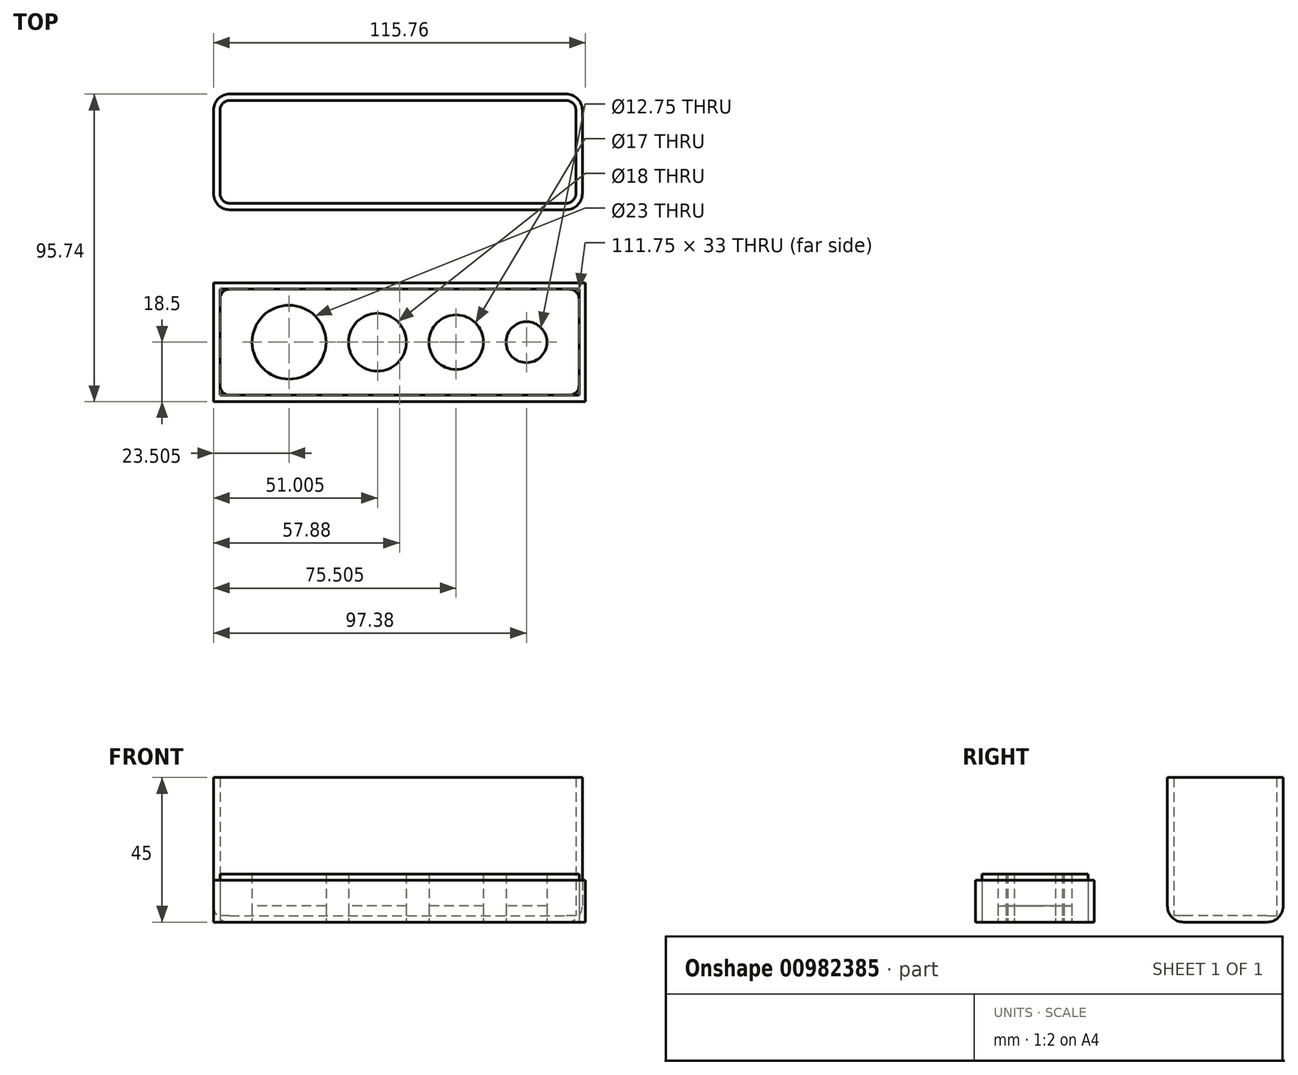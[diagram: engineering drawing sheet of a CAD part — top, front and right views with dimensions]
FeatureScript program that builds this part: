
annotation { "Feature Type Name" : "Feature", "Feature Type Description" : "" }
export const myFeature = defineFeature(function(context is Context, id is Id, definition is map)
    precondition{}
    {
        {
            var Q0;
            Q0=qCreatedBy(makeId("Top.planeOp"),FACE);
            var sketch = newSketch(context, id + "F0", { "sketchPlane" : qUnion([Q0])});
            skLineSegment(sketch, "E0.bottom", {"start": v(-55.88, 35) * mm, "end": v(55.87, 35) * mm});
            skLineSegment(sketch, "E0.top", {"start": v(-55.88, 2) * mm, "end": v(55.87, 2) * mm});
            skLineSegment(sketch, "E0.left", {"start": v(-55.88, 35) * mm, "end": v(-55.88, 2) * mm});
            skLineSegment(sketch, "E0.right", {"start": v(55.87, 35) * mm, "end": v(55.87, 2) * mm});
            skCircle(sketch, "E1", {"center": v(-34.38, 18.5) * mm, "radius": 11.5 * mm});
            skCircle(sketch, "E2", {"center": v(-6.88, 18.5) * mm, "radius": 9 * mm});
            skCircle(sketch, "E3", {"center": v(17.62, 18.5) * mm, "radius": 8.5 * mm});
            skCircle(sketch, "E4", {"center": v(39.5, 18.5) * mm, "radius": 6.38 * mm});
            skLineSegment(sketch, "E5.bottom", {"start": v(-57.88, 37) * mm, "end": v(57.88, 37) * mm});
            skLineSegment(sketch, "E5.top", {"start": v(-57.88, 0) * mm, "end": v(57.88, 0) * mm});
            skLineSegment(sketch, "E5.left", {"start": v(-57.88, 37) * mm, "end": v(-57.88, 0) * mm});
            skLineSegment(sketch, "E5.right", {"start": v(57.88, 37) * mm, "end": v(57.88, 0) * mm});
            skPoint(sketch, "E6", {"position": v(0, 37) * mm});
            skSolve(sketch);
        }
        {
            var Q0;
            Q0=makeQuery(id+"F0.imprint","IMPRINT",FACE,{"disambiguationData":[TD([[makeQuery(id+"F0.imprint","IMPRINT",EDGE,{"derivedFrom":sQuery(id+"F0.wireOp",EDGE,"E1")}),1.0]])]});
            var Q1;
            Q1=makeQuery(id+"F0.imprint","IMPRINT",FACE,{"disambiguationData":[TD([[makeQuery(id+"F0.imprint","IMPRINT",EDGE,{"derivedFrom":sQuery(id+"F0.wireOp",EDGE,"E2")}),1.0]])]});
            var Q2;
            Q2=makeQuery(id+"F0.imprint","IMPRINT",FACE,{"disambiguationData":[TD([[makeQuery(id+"F0.imprint","IMPRINT",EDGE,{"derivedFrom":sQuery(id+"F0.wireOp",EDGE,"E3")}),1.0]])]});
            var Q3;
            Q3=makeQuery(id+"F0.imprint","IMPRINT",FACE,{"disambiguationData":[TD([[makeQuery(id+"F0.imprint","IMPRINT",EDGE,{"derivedFrom":sQuery(id+"F0.wireOp",EDGE,"E4")}),1.0]])]});
            extrude(context, id + "F1", {"entities" : qUnion([Q0, Q1, Q2, Q3]), "depth" : 5 * mm, "offsetDistance" : 25 * mm});
        }
        {
            var Q0;
            Q0=makeQuery(id+"F0.imprint","IMPRINT",FACE,{"disambiguationData":[TD([[makeQuery(id+"F0.imprint","IMPRINT",EDGE,{"derivedFrom":sQuery(id+"F0.wireOp",EDGE,"E0.bottom")}),1.0]])]});
            extrude(context, id + "F2", {"entities" : qUnion([Q0]), "depth" : 13 * mm, "offsetDistance" : 25 * mm});
        }
        {
            var Q0;
            Q0=makeQuery(id+"F0.imprint","IMPRINT",FACE,{"disambiguationData":[TD([[makeQuery(id+"F0.imprint","IMPRINT",EDGE,{"derivedFrom":sQuery(id+"F0.wireOp",EDGE,"E0.bottom")}),-1.0]])]});
            extrude(context, id + "F3", {"entities" : qUnion([Q0]), "depth" : 15 * mm, "offsetDistance" : 25 * mm});
        }
        {
            var Q0;
            Q0=qCreatedBy(makeId("Top.planeOp"),FACE);
            var sketch = newSketch(context, id + "F4", { "sketchPlane" : qUnion([Q0])});
            skLineSegment(sketch, "E7.bottom", {"start": v(-57.88, -4.26) * mm, "end": v(56.88, -4.26) * mm});
            skLineSegment(sketch, "E7.top", {"start": v(-57.87, -40.26) * mm, "end": v(56.88, -40.26) * mm});
            skLineSegment(sketch, "E7.left", {"start": v(-57.88, -4.26) * mm, "end": v(-57.88, -40.26) * mm});
            skLineSegment(sketch, "E7.right", {"start": v(56.88, -4.26) * mm, "end": v(56.88, -40.26) * mm});
            skLineSegment(sketch, "E8.bottom", {"start": v(-55.88, -6.26) * mm, "end": v(54.88, -6.26) * mm});
            skLineSegment(sketch, "E8.top", {"start": v(-55.88, -38.26) * mm, "end": v(54.88, -38.26) * mm});
            skLineSegment(sketch, "E8.left", {"start": v(-55.88, -6.26) * mm, "end": v(-55.88, -38.26) * mm});
            skLineSegment(sketch, "E8.right", {"start": v(54.88, -6.26) * mm, "end": v(54.88, -38.26) * mm});
            skSolve(sketch);
        }
        {
            var Q0;
            Q0=makeQuery(id+"F4.imprint","IMPRINT",FACE,{"disambiguationData":[TD([[makeQuery(id+"F4.imprint","IMPRINT",EDGE,{"derivedFrom":sQuery(id+"F4.wireOp",EDGE,"E8.bottom")}),-1.0]])]});
            extrude(context, id + "F5", {"entities" : qUnion([Q0]), "depth" : 2 * mm, "offsetDistance" : 25 * mm});
        }
        {
            var Q0;
            Q0=makeQuery(id+"F4.imprint","IMPRINT",FACE,{"disambiguationData":[TD([[makeQuery(id+"F4.imprint","IMPRINT",EDGE,{"derivedFrom":sQuery(id+"F4.wireOp",EDGE,"E7.bottom")}),-1.0]])]});
            extrude(context, id + "F6", {"entities" : qUnion([Q0]), "operationType" : NewBodyOperationType.ADD, "depth" : 45 * mm, "offsetDistance" : 25 * mm});
        }
        {
            var Q0;
            Q0=makeQuery(id+"F2.opExtrude","SWEPT_EDGE",EDGE,{"disambiguationData":[OSD([sQuery(id+"F0.wireOp",EDGE,"E5.bottom"),sQuery(id+"F0.wireOp",EDGE,"E5.left")])]});
            var Q1;
            Q1=makeQuery(id+"F2.opExtrude","SWEPT_EDGE",EDGE,{"disambiguationData":[OSD([sQuery(id+"F0.wireOp",EDGE,"E5.top"),sQuery(id+"F0.wireOp",EDGE,"E5.left")])]});
            var Q2;
            Q2=makeQuery(id+"F2.opExtrude","SWEPT_EDGE",EDGE,{"disambiguationData":[OSD([sQuery(id+"F0.wireOp",EDGE,"E5.top"),sQuery(id+"F0.wireOp",EDGE,"E5.right")])]});
            var Q3;
            Q3=makeQuery(id+"F2.opExtrude","SWEPT_EDGE",EDGE,{"disambiguationData":[OSD([sQuery(id+"F0.wireOp",EDGE,"E5.bottom"),sQuery(id+"F0.wireOp",EDGE,"E5.right")])]});
            var Q4;
            Q4=makeQuery(id+"F2.opExtrude","CAP_EDGE",EDGE,{"disambiguationData":[OSD([sQuery(id+"F0.wireOp",EDGE,"E5.bottom")])],"isStart":true});
            var Q5;
            Q5=makeQuery(id+"F2.opExtrude","CAP_EDGE",EDGE,{"disambiguationData":[OSD([sQuery(id+"F0.wireOp",EDGE,"E5.right")])],"isStart":true});
            var Q6;
            Q6=makeQuery(id+"F2.opExtrude","CAP_EDGE",EDGE,{"disambiguationData":[OSD([sQuery(id+"F0.wireOp",EDGE,"E5.top")])],"isStart":true});
            var Q7;
            Q7=makeQuery(id+"F2.opExtrude","CAP_EDGE",EDGE,{"disambiguationData":[OSD([sQuery(id+"F0.wireOp",EDGE,"E5.left")])],"isStart":true});
            var Q8;
            Q8=makeQuery(id+"F6.opExtrude","SWEPT_EDGE",EDGE,{"disambiguationData":[OSD([sQuery(id+"F4.wireOp",EDGE,"E7.bottom"),sQuery(id+"F4.wireOp",EDGE,"E7.right")])]});
            var Q9;
            Q9=makeQuery(id+"F6.opExtrude","SWEPT_EDGE",EDGE,{"disambiguationData":[OSD([sQuery(id+"F4.wireOp",EDGE,"E7.top"),sQuery(id+"F4.wireOp",EDGE,"E7.right")])]});
            var Q10;
            Q10=makeQuery(id+"F6.opExtrude","SWEPT_EDGE",EDGE,{"disambiguationData":[OSD([sQuery(id+"F4.wireOp",EDGE,"E7.bottom"),sQuery(id+"F4.wireOp",EDGE,"E7.left")])]});
            var Q11;
            Q11=makeQuery(id+"F6.opExtrude","SWEPT_EDGE",EDGE,{"disambiguationData":[OSD([sQuery(id+"F4.wireOp",EDGE,"E7.top"),sQuery(id+"F4.wireOp",EDGE,"E7.left")])]});
            var Q12;
            Q12=makeQuery(id+"F6.opExtrude","CAP_EDGE",EDGE,{"disambiguationData":[OSD([sQuery(id+"F4.wireOp",EDGE,"E7.left")])],"isStart":true});
            var Q13;
            Q13=makeQuery(id+"F6.opExtrude","CAP_EDGE",EDGE,{"disambiguationData":[OSD([sQuery(id+"F4.wireOp",EDGE,"E7.right")])],"isStart":true});
            fillet(context, id + "F7", {"entities" : qUnion([Q0, Q1, Q2, Q3, Q4, Q5, Q6, Q7, Q8, Q9, Q10, Q11, Q12, Q13]), "radius" : 5 * mm, "tangentPropagation" : true, "allowEdgeOverflow" : false});
        }
        {
            var Q0;
            Q0=makeQuery(id+"F3.opExtrude","SWEPT_EDGE",EDGE,{"disambiguationData":[OSD([sQuery(id+"F0.wireOp",EDGE,"E0.bottom"),sQuery(id+"F0.wireOp",EDGE,"E0.right")])]});
            var Q1;
            Q1=makeQuery(id+"F3.opExtrude","SWEPT_EDGE",EDGE,{"disambiguationData":[OSD([sQuery(id+"F0.wireOp",EDGE,"E0.top"),sQuery(id+"F0.wireOp",EDGE,"E0.right")])]});
            var Q2;
            Q2=makeQuery(id+"F3.opExtrude","SWEPT_EDGE",EDGE,{"disambiguationData":[OSD([sQuery(id+"F0.wireOp",EDGE,"E0.bottom"),sQuery(id+"F0.wireOp",EDGE,"E0.left")])]});
            var Q3;
            Q3=makeQuery(id+"F3.opExtrude","SWEPT_EDGE",EDGE,{"disambiguationData":[OSD([sQuery(id+"F0.wireOp",EDGE,"E0.top"),sQuery(id+"F0.wireOp",EDGE,"E0.left")])]});
            var Q4;
            Q4=makeQuery(id+"F6.opExtrude","SWEPT_EDGE",EDGE,{"disambiguationData":[OSD([sQuery(id+"F4.wireOp",EDGE,"E8.top"),sQuery(id+"F4.wireOp",EDGE,"E8.left")])]});
            var Q5;
            Q5=makeQuery(id+"F6.opExtrude","SWEPT_EDGE",EDGE,{"disambiguationData":[OSD([sQuery(id+"F4.wireOp",EDGE,"E8.bottom"),sQuery(id+"F4.wireOp",EDGE,"E8.left")])]});
            var Q6;
            Q6=makeQuery(id+"F6.opExtrude","SWEPT_EDGE",EDGE,{"disambiguationData":[OSD([sQuery(id+"F4.wireOp",EDGE,"E8.top"),sQuery(id+"F4.wireOp",EDGE,"E8.right")])]});
            var Q7;
            Q7=makeQuery(id+"F6.opExtrude","SWEPT_EDGE",EDGE,{"disambiguationData":[OSD([sQuery(id+"F4.wireOp",EDGE,"E8.bottom"),sQuery(id+"F4.wireOp",EDGE,"E8.right")])]});
            var Q8;
            Q8=makeQuery(id+"F5.opExtrude","CAP_EDGE",EDGE,{"disambiguationData":[OSD([sQuery(id+"F4.wireOp",EDGE,"E8.bottom")])],"isStart":false});
            var Q9;
            Q9=makeQuery(id+"F5.opExtrude","CAP_EDGE",EDGE,{"disambiguationData":[OSD([sQuery(id+"F4.wireOp",EDGE,"E8.top")])],"isStart":false});
            var Q10;
            Q10=makeQuery(id+"F5.opExtrude","CAP_EDGE",EDGE,{"disambiguationData":[OSD([sQuery(id+"F4.wireOp",EDGE,"E8.left")])],"isStart":false});
            var Q11;
            Q11=makeQuery(id+"F5.opExtrude","CAP_EDGE",EDGE,{"disambiguationData":[OSD([sQuery(id+"F4.wireOp",EDGE,"E8.right")])],"isStart":false});
            fillet(context, id + "F8", {"entities" : qUnion([Q0, Q1, Q2, Q3, Q4, Q5, Q6, Q7, Q8, Q9, Q10, Q11]), "radius" : 3 * mm, "tangentPropagation" : true, "allowEdgeOverflow" : false});
        }
        {
            var Q0;
            Q0=makeQuery(id+"F5.opExtrude","SWEPT_BODY",BODY,{"disambiguationData":[OSD([sQuery(id+"F4.wireOp",EDGE,"E8.bottom"),sQuery(id+"F4.wireOp",EDGE,"E8.top"),sQuery(id+"F4.wireOp",EDGE,"E8.left"),sQuery(id+"F4.wireOp",EDGE,"E8.right")])]});
            transform(context, id + "F9", {"entities" : qUnion([Q0]), "transformType" : TransformType.TRANSLATION_3D, "dx" : 0 * mm, "dy" : 100 * mm, "dz" : 0 * mm, "makeCopy" : false});
        }
        {
            var Q0;
            Q0=makeQuery(id+"F6.opExtrude","CAP_EDGE",EDGE,{"disambiguationData":[OSD([sQuery(id+"F4.wireOp",EDGE,"E7.bottom")])],"isStart":true});
            var Q1;
            Q1=makeQuery(id+"F6.opExtrude","CAP_EDGE",EDGE,{"disambiguationData":[OSD([sQuery(id+"F4.wireOp",EDGE,"E7.top")])],"isStart":true});
            fillet(context, id + "F10", {"entities" : qUnion([Q0, Q1]), "radius" : 5 * mm, "tangentPropagation" : true, "allowEdgeOverflow" : false});
        }
    });
